# Revit family: Glidehylse_LD_16_Part_S_A4_p_i_t_4031209
name_source: partatom
category: Generic Models
units: mm (PartAtom-declared; Revit-internal decimal feet)

## family parameters
Always vertical = No
Can host rebar = No
Cut with Voids When Loaded = No
Part Type = Normal
Room Calculation Point = No
Round Connector Dimension = Use Diameter
Shared = No
Work Plane-Based = Yes

## types (2) — shared parameters
Cap Height = 5 mm  [stored 0.0164042 ft]
Default Elevation = 1219 mm
Elevation Height = 100 mm  [stored 0.328084 ft]
Hexagon Diameter = 80 mm  [stored 0.262467 ft]
Hexagon Height = 5 mm  [stored 0.0164042 ft]
Metal = Steel A4
Plastic Black = Plastic Black
Technical Data Sheet = https://haucon.dk
Website Link = https://haucon.dk

## per-type parameters (varying)
| type | Plastic | Sleeve Inner Diameter | Total Length |
| LD16_Part_S_A4 | PVC, Flexible | 17 mm | 195 mm  [stored 0.639764 ft] |
| LD20_Part_S_A4 | Plastic Blue | 21 mm  [stored 0.0688976 ft] | 220 mm  [stored 0.721785 ft] |

note: [stored X ft] marks values corroborated as IEEE doubles in the binary element streams (Revit-internal decimal feet)

## geometry (parser evidence)
native form markers: Sweep x2
no freeform markers — native parametric forms only
